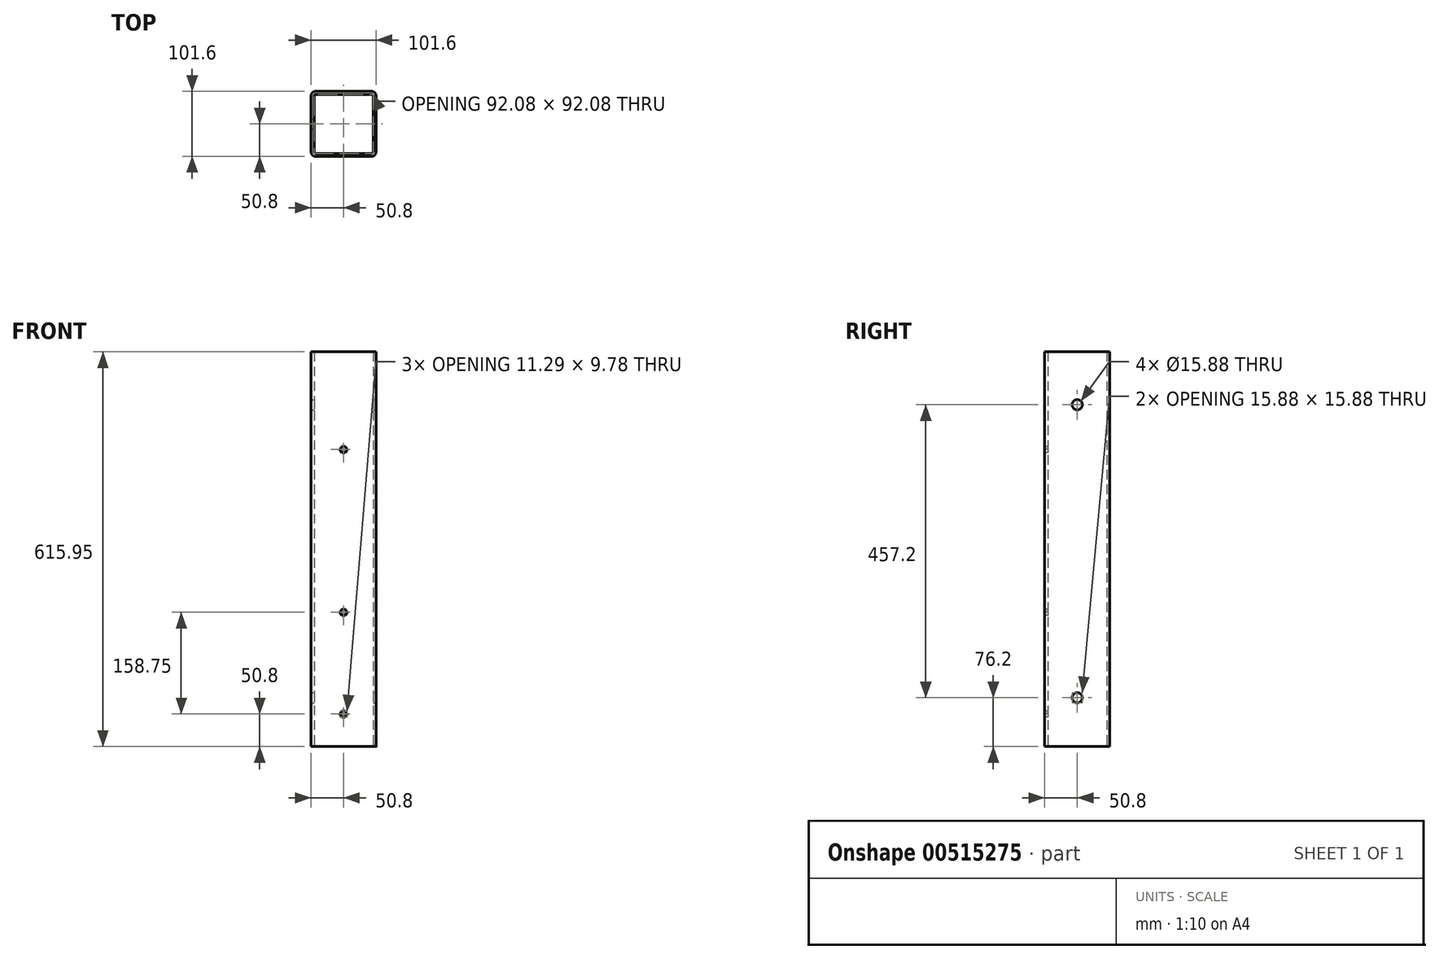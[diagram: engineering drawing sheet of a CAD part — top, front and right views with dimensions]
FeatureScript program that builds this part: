
annotation { "Feature Type Name" : "Feature", "Feature Type Description" : "" }
export const myFeature = defineFeature(function(context is Context, id is Id, definition is map)
    precondition{}
    {
        {
            var Q0;
            Q0=qCreatedBy(makeId("Top.planeOp"),FACE);
            var sketch = newSketch(context, id + "F0", { "sketchPlane" : qUnion([Q0])});
            skLineSegment(sketch, "E0.bottom", {"start": v(-43.66, 50.8) * mm, "end": v(43.66, 50.8) * mm});
            skLineSegment(sketch, "E0.top", {"start": v(-43.66, -50.8) * mm, "end": v(43.66, -50.8) * mm});
            skLineSegment(sketch, "E0.left", {"start": v(-50.8, 43.66) * mm, "end": v(-50.8, -43.66) * mm});
            skLineSegment(sketch, "E0.right", {"start": v(50.8, 43.66) * mm, "end": v(50.8, -43.66) * mm});
            skPoint(sketch, "E1.visualSharp", {"position": v(50.8, 50.8) * mm});
            skArc(sketch, "E1.filletArc", {"start": v(50.8, 43.66) * mm, "mid": v(48.7, 48.7) * mm, "end": v(43.66, 50.8) * mm});
            skPoint(sketch, "E2.visualSharp", {"position": v(-50.8, 50.8) * mm});
            skArc(sketch, "E2.filletArc", {"start": v(-43.66, 50.8) * mm, "mid": v(-48.7, 48.7) * mm, "end": v(-50.8, 43.66) * mm});
            skPoint(sketch, "E3.visualSharp", {"position": v(-50.8, -50.8) * mm});
            skArc(sketch, "E3.filletArc", {"start": v(-50.8, -43.66) * mm, "mid": v(-48.7, -48.7) * mm, "end": v(-43.66, -50.8) * mm});
            skPoint(sketch, "E4.visualSharp", {"position": v(50.8, -50.8) * mm});
            skArc(sketch, "E4.filletArc", {"start": v(43.66, -50.8) * mm, "mid": v(48.7, -48.7) * mm, "end": v(50.8, -43.66) * mm});
            skLineSegment(sketch, "E5.bottom", {"start": v(-43.66, -46.04) * mm, "end": v(43.66, -46.04) * mm});
            skLineSegment(sketch, "E5.top", {"start": v(-43.66, 46.04) * mm, "end": v(43.66, 46.04) * mm});
            skLineSegment(sketch, "E5.left", {"start": v(-46.04, -43.66) * mm, "end": v(-46.04, 43.66) * mm});
            skLineSegment(sketch, "E5.right", {"start": v(46.04, -43.66) * mm, "end": v(46.04, 43.66) * mm});
            skPoint(sketch, "E5.middle", {"position": v(0, 0) * mm});
            skPoint(sketch, "E6.visualSharp", {"position": v(46.04, 46.04) * mm});
            skArc(sketch, "E6.filletArc", {"start": v(46.04, 43.66) * mm, "mid": v(45.34, 45.34) * mm, "end": v(43.66, 46.04) * mm});
            skPoint(sketch, "E7.visualSharp", {"position": v(-46.04, 46.04) * mm});
            skArc(sketch, "E7.filletArc", {"start": v(-43.66, 46.04) * mm, "mid": v(-45.34, 45.34) * mm, "end": v(-46.04, 43.66) * mm});
            skPoint(sketch, "E8.visualSharp", {"position": v(-46.04, -46.04) * mm});
            skArc(sketch, "E8.filletArc", {"start": v(-46.04, -43.66) * mm, "mid": v(-45.34, -45.34) * mm, "end": v(-43.66, -46.04) * mm});
            skPoint(sketch, "E9.visualSharp", {"position": v(46.04, -46.04) * mm});
            skArc(sketch, "E9.filletArc", {"start": v(43.66, -46.04) * mm, "mid": v(45.34, -45.34) * mm, "end": v(46.04, -43.66) * mm});
            skLineSegment(sketch, "E10", {"start": v(0, 50.8) * mm, "end": v(0, -50.8) * mm, "construction": true});
            skLineSegment(sketch, "E11", {"start": v(-50.8, 0) * mm, "end": v(50.8, 0) * mm, "construction": true});
            skSolve(sketch);
        }
        {
            var Q0;
            Q0=qSketchRegion(id+"F0",true);
            extrude(context, id + "F1", {"entities" : qUnion([Q0]), "depth" : 615.95 * mm, "offsetDistance" : 25.4 * mm});
        }
        {
            var Q0;
            Q0=makeQuery(id+"F1.opExtrude","SWEPT_FACE",FACE,{"disambiguationData":[OSD([sQuery(id+"F0.wireOp",EDGE,"E0.top")])]});
            var sketch = newSketch(context, id + "F2", { "sketchPlane" : qUnion([Q0])});
            skCircle(sketch, "E12.cCircle", {"center": v(0, 50.8) * mm, "radius": 4.89 * mm, "construction": true});
            skLineSegment(sketch, "E12.0", {"start": v(2.82, 45.91) * mm, "end": v(-2.82, 45.91) * mm});
            skLineSegment(sketch, "E12.1", {"start": v(-2.82, 45.91) * mm, "end": v(-5.65, 50.8) * mm});
            skLineSegment(sketch, "E12.2", {"start": v(-5.65, 50.8) * mm, "end": v(-2.82, 55.69) * mm});
            skLineSegment(sketch, "E12.3", {"start": v(-2.82, 55.69) * mm, "end": v(2.82, 55.69) * mm});
            skLineSegment(sketch, "E12.4", {"start": v(2.82, 55.69) * mm, "end": v(5.65, 50.8) * mm});
            skLineSegment(sketch, "E12.5", {"start": v(5.65, 50.8) * mm, "end": v(2.82, 45.91) * mm});
            skPoint(sketch, "E12.0.midPoint", {"position": v(0, 45.91) * mm});
            skCircle(sketch, "E13.cCircle", {"center": v(0, 209.55) * mm, "radius": 4.89 * mm, "construction": true});
            skLineSegment(sketch, "E13.0", {"start": v(2.82, 204.66) * mm, "end": v(-2.82, 204.66) * mm});
            skLineSegment(sketch, "E13.1", {"start": v(-2.82, 204.66) * mm, "end": v(-5.65, 209.55) * mm});
            skLineSegment(sketch, "E13.2", {"start": v(-5.65, 209.55) * mm, "end": v(-2.82, 214.44) * mm});
            skLineSegment(sketch, "E13.3", {"start": v(-2.82, 214.44) * mm, "end": v(2.82, 214.44) * mm});
            skLineSegment(sketch, "E13.4", {"start": v(2.82, 214.44) * mm, "end": v(5.65, 209.55) * mm});
            skLineSegment(sketch, "E13.5", {"start": v(5.65, 209.55) * mm, "end": v(2.82, 204.66) * mm});
            skPoint(sketch, "E13.0.midPoint", {"position": v(0, 204.66) * mm});
            skCircle(sketch, "E14.cCircle", {"center": v(0, 463.55) * mm, "radius": 4.89 * mm, "construction": true});
            skLineSegment(sketch, "E14.0", {"start": v(2.82, 458.66) * mm, "end": v(-2.82, 458.66) * mm});
            skLineSegment(sketch, "E14.1", {"start": v(-2.82, 458.66) * mm, "end": v(-5.65, 463.55) * mm});
            skLineSegment(sketch, "E14.2", {"start": v(-5.65, 463.55) * mm, "end": v(-2.82, 468.44) * mm});
            skLineSegment(sketch, "E14.3", {"start": v(-2.82, 468.44) * mm, "end": v(2.82, 468.44) * mm});
            skLineSegment(sketch, "E14.4", {"start": v(2.82, 468.44) * mm, "end": v(5.65, 463.55) * mm});
            skLineSegment(sketch, "E14.5", {"start": v(5.65, 463.55) * mm, "end": v(2.82, 458.66) * mm});
            skPoint(sketch, "E14.0.midPoint", {"position": v(0, 458.66) * mm});
            skSolve(sketch);
        }
        {
            var Q0;
            Q0 = qSketchRegion(id + "F2", true);
            extrude(context, id + "F3", {"entities" : qUnion([Q0]), "operationType" : NewBodyOperationType.REMOVE, "oppositeDirection" : true, "depth" : 25.4 * mm, "offsetDistance" : 25.4 * mm});
        }
        {
            var Q0;
            Q0=makeQuery(id+"F1.opExtrude","SWEPT_FACE",FACE,{"disambiguationData":[OSD([sQuery(id+"F0.wireOp",EDGE,"E0.right")])]});
            var sketch = newSketch(context, id + "F4", { "sketchPlane" : qUnion([Q0])});
            skCircle(sketch, "E15", {"center": v(0, 76.2) * mm, "radius": 7.94 * mm});
            skCircle(sketch, "E16", {"center": v(0, 533.4) * mm, "radius": 7.94 * mm});
            skSolve(sketch);
        }
        {
            var Q0;
            Q0 = qSketchRegion(id + "F4", true);
            extrude(context, id + "F5", {"entities" : qUnion([Q0]), "operationType" : NewBodyOperationType.REMOVE, "endBound" : BoundingType.THROUGH_ALL, "oppositeDirection" : true, "depth" : 25.4 * mm, "offsetDistance" : 25.4 * mm});
        }
    });
